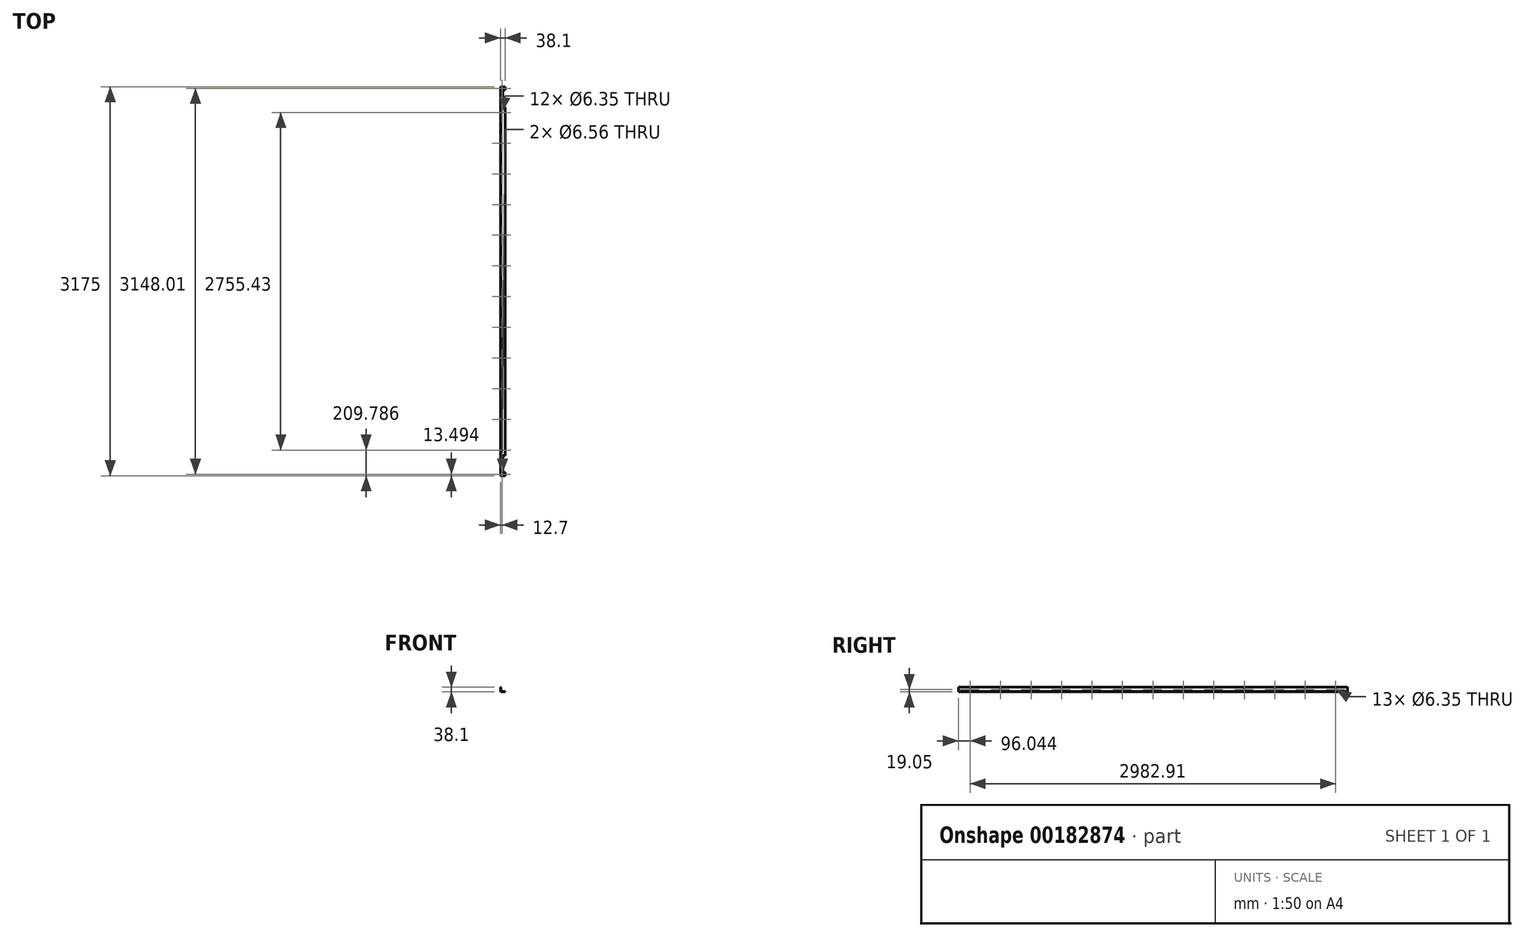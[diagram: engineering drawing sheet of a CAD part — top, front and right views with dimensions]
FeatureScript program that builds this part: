
annotation { "Feature Type Name" : "Feature", "Feature Type Description" : "" }
export const myFeature = defineFeature(function(context is Context, id is Id, definition is map)
    precondition{}
    {
        {
            var Q0;
            Q0=qCreatedBy(makeId("Front.planeOp"),FACE);
            var sketch = newSketch(context, id + "F0", { "sketchPlane" : qUnion([Q0])});
            skLineSegment(sketch, "E0.bottom", {"start": v(0, 0) * mm, "end": v(38.1, 0) * mm});
            skLineSegment(sketch, "E0.top", {"start": v(3.18, 3.17) * mm, "end": v(38.1, 3.17) * mm});
            skLineSegment(sketch, "E0.right", {"start": v(38.1, 0) * mm, "end": v(38.1, 3.17) * mm});
            skLineSegment(sketch, "E1.top", {"start": v(0, 38.1) * mm, "end": v(3.17, 38.1) * mm});
            skLineSegment(sketch, "E1.left", {"start": v(0, 0) * mm, "end": v(0, 38.1) * mm});
            skLineSegment(sketch, "E1.right", {"start": v(3.18, 3.17) * mm, "end": v(3.17, 38.1) * mm});
            skSolve(sketch);
        }
        {
            var Q0;
            Q0=makeQuery(id+"F0.imprint","IMPRINT",FACE,{"disambiguationData":[TD([[makeQuery(id+"F0.imprint","IMPRINT",EDGE,{"derivedFrom":sQuery(id+"F0.wireOp",EDGE,"E0.bottom")}),1.0]])]});
            extrude(context, id + "F1", {"entities" : qUnion([Q0]), "oppositeDirection" : true, "depth" : 3175 * mm});
        }
        {
            var Q0;
            Q0=qCreatedBy(makeId("Top.planeOp"),FACE);
            var sketch = newSketch(context, id + "F2", { "sketchPlane" : qUnion([Q0])});
            skLineSegment(sketch, "E2.bottom", {"start": v(38.1, 26.99) * mm, "end": v(20.64, 26.99) * mm});
            skLineSegment(sketch, "E2.top", {"start": v(38.1, 165.1) * mm, "end": v(20.64, 165.1) * mm});
            skLineSegment(sketch, "E2.left", {"start": v(38.1, 26.99) * mm, "end": v(38.1, 165.1) * mm});
            skLineSegment(sketch, "E2.right", {"start": v(20.64, 26.99) * mm, "end": v(20.64, 165.1) * mm});
            skCircle(sketch, "E3", {"center": v(12.7, 13.5) * mm, "radius": 3.28 * mm});
            skLineSegment(sketch, "E4", {"start": v(38.1, 1587.5) * mm, "end": v(-39.32, 1587.5) * mm, "construction": true});
            skLineSegment(sketch, "E5", {"start": v(20.64, 26.99) * mm, "end": v(20.64, 0) * mm, "construction": true});
            skLineSegment(sketch, "E6", {"start": v(49.67, 13.5) * mm, "end": v(-10.61, 13.5) * mm, "construction": true});
            skPoint(sketch, "E6.startSnap0", {"position": v(20.64, 13.5) * mm});
            skCircle(sketch, "E7.0.1.0", {"center": v(12.7, 209.79) * mm, "radius": 3.28 * mm});
            skCircle(sketch, "E7.0.2.0", {"center": v(12.7, 554.21) * mm, "radius": 3.28 * mm});
            skCircle(sketch, "E7.0.3.0", {"center": v(12.7, 898.64) * mm, "radius": 3.28 * mm});
            skCircle(sketch, "E7.0.4.0", {"center": v(12.7, 1243.07) * mm, "radius": 3.28 * mm});
            skCircle(sketch, "E7.0.5.0", {"center": v(12.7, 1587.5) * mm, "radius": 3.28 * mm});
            skLineSegment(sketch, "E7.direction1", {"start": v(12.7, 13.5) * mm, "end": v(55.73, 13.5) * mm, "construction": true});
            skLineSegment(sketch, "E7.direction2", {"start": v(12.7, 13.5) * mm, "end": v(12.7, 209.79) * mm, "construction": true});
            skLineSegment(sketch, "E8", {"start": v(12.7, 1587.5) * mm, "end": v(12.7, 1243.07) * mm});
            skLineSegment(sketch, "E9", {"start": v(12.7, 898.64) * mm, "end": v(12.7, 554.21) * mm});
            skLineSegment(sketch, "E10", {"start": v(12.7, 209.79) * mm, "end": v(12.7, 554.21) * mm});
            skLineSegment(sketch, "E11", {"start": v(12.7, 898.64) * mm, "end": v(12.7, 1243.07) * mm});
            skCircle(sketch, "E12.MirrorC", {"center": v(12.7, 1931.93) * mm, "radius": 3.28 * mm});
            skCircle(sketch, "E13.MirrorC", {"center": v(12.7, 2276.36) * mm, "radius": 3.28 * mm});
            skCircle(sketch, "E14.MirrorC", {"center": v(12.7, 2620.79) * mm, "radius": 3.28 * mm});
            skCircle(sketch, "E15.MirrorC", {"center": v(12.7, 2965.21) * mm, "radius": 3.28 * mm});
            skCircle(sketch, "E16.MirrorC", {"center": v(12.7, 3161.5) * mm, "radius": 3.28 * mm});
            skLineSegment(sketch, "E17.MirrorCS", {"start": v(38.1, 3148.01) * mm, "end": v(20.64, 3148.01) * mm});
            skLineSegment(sketch, "E18.MirrorCS", {"start": v(20.64, 3148.01) * mm, "end": v(20.64, 3009.9) * mm});
            skLineSegment(sketch, "E19.MirrorCS", {"start": v(38.1, 3148.01) * mm, "end": v(38.1, 3009.9) * mm});
            skLineSegment(sketch, "E20.MirrorCS", {"start": v(38.1, 3009.9) * mm, "end": v(20.64, 3009.9) * mm});
            skSolve(sketch);
        }
        {
            var Q0;
            Q0=qCreatedBy(makeId("Right.planeOp"),FACE);
            var sketch = newSketch(context, id + "F3", { "sketchPlane" : qUnion([Q0])});
            skLineSegment(sketch, "E21", {"start": v(57.42, 79.6) * mm, "end": v(57.42, -13.2) * mm, "construction": true});
            skCircle(sketch, "E22", {"center": v(79.28, 20.64) * mm, "radius": 3.18 * mm});
            skCircle(sketch, "E23", {"center": v(463.9, 20.64) * mm, "radius": 3.18 * mm});
            skLineSegment(sketch, "E24", {"start": v(838.44, 20.64) * mm, "end": v(463.9, 20.64) * mm, "construction": true});
            skLineSegment(sketch, "E25", {"start": v(838.44, 20.64) * mm, "end": v(1212.97, 20.64) * mm, "construction": true});
            skLineSegment(sketch, "E26", {"start": v(1212.97, 20.64) * mm, "end": v(1587.5, 20.64) * mm, "construction": true});
            skLineSegment(sketch, "E27", {"start": v(1587.5, 20.64) * mm, "end": v(1962.03, 20.64) * mm, "construction": true});
            skCircle(sketch, "E28", {"center": v(838.44, 20.64) * mm, "radius": 3.18 * mm});
            skCircle(sketch, "E29", {"center": v(1212.97, 20.64) * mm, "radius": 3.18 * mm});
            skCircle(sketch, "E30", {"center": v(1587.5, 20.64) * mm, "radius": 3.18 * mm});
            skCircle(sketch, "E31", {"center": v(1962.03, 20.64) * mm, "radius": 3.18 * mm});
            skLineSegment(sketch, "E32", {"start": v(1962.03, 20.64) * mm, "end": v(2336.56, 20.64) * mm, "construction": true});
            skLineSegment(sketch, "E33", {"start": v(2336.56, 20.64) * mm, "end": v(2730.13, 20.64) * mm, "construction": true});
            skCircle(sketch, "E34", {"center": v(2336.56, 20.64) * mm, "radius": 3.17 * mm});
            skCircle(sketch, "E35", {"center": v(2730.13, 20.64) * mm, "radius": 3.17 * mm});
            skLineSegment(sketch, "E36", {"start": v(3047.86, 3.17) * mm, "end": v(3047.86, 38.1) * mm, "construction": true});
            skLineSegment(sketch, "E37", {"start": v(2730.13, 20.64) * mm, "end": v(2903.64, 21.22) * mm});
            skSolve(sketch);
        }
        {
            var Q0;
            Q0=qCreatedBy(makeId("Right.planeOp"),FACE);
            var sketch = newSketch(context, id + "F4", { "sketchPlane" : qUnion([Q0])});
            skLineSegment(sketch, "E38", {"start": v(427.48, 19.05) * mm, "end": v(758.91, 19.05) * mm, "construction": true});
            skLineSegment(sketch, "E39", {"start": v(96.04, 19.05) * mm, "end": v(427.48, 19.05) * mm, "construction": true});
            skLineSegment(sketch, "E40", {"start": v(758.91, 19.05) * mm, "end": v(1090.35, 19.05) * mm, "construction": true});
            skLineSegment(sketch, "E41", {"start": v(1090.35, 19.05) * mm, "end": v(1421.78, 19.05) * mm, "construction": true});
            skLineSegment(sketch, "E42", {"start": v(1421.78, 19.05) * mm, "end": v(1753.22, 19.05) * mm, "construction": true});
            skLineSegment(sketch, "E43", {"start": v(1753.22, 19.05) * mm, "end": v(2084.65, 19.05) * mm, "construction": true});
            skLineSegment(sketch, "E44", {"start": v(2084.65, 19.05) * mm, "end": v(2416.09, 19.05) * mm, "construction": true});
            skLineSegment(sketch, "E45", {"start": v(2416.09, 19.05) * mm, "end": v(2747.52, 19.05) * mm, "construction": true});
            skLineSegment(sketch, "E46", {"start": v(96.04, 87.6) * mm, "end": v(3078.96, 87.6) * mm, "construction": true});
            skLineSegment(sketch, "E47", {"start": v(3078.96, -671.36) * mm, "end": v(3078.96, 846.57) * mm, "construction": true});
            skCircle(sketch, "E48", {"center": v(758.91, 19.05) * mm, "radius": 3.18 * mm});
            skCircle(sketch, "E49", {"center": v(427.48, 19.05) * mm, "radius": 3.18 * mm});
            skCircle(sketch, "E50", {"center": v(96.04, 19.05) * mm, "radius": 3.18 * mm});
            skCircle(sketch, "E51", {"center": v(1090.35, 19.05) * mm, "radius": 3.18 * mm});
            skCircle(sketch, "E52", {"center": v(1421.78, 19.05) * mm, "radius": 3.18 * mm});
            skCircle(sketch, "E53", {"center": v(1753.22, 19.05) * mm, "radius": 3.18 * mm});
            skCircle(sketch, "E54", {"center": v(2084.65, 19.05) * mm, "radius": 3.18 * mm});
            skCircle(sketch, "E55", {"center": v(2416.09, 19.05) * mm, "radius": 3.18 * mm});
            skCircle(sketch, "E56", {"center": v(2747.52, 19.05) * mm, "radius": 3.18 * mm});
            skLineSegment(sketch, "E57", {"start": v(1587.5, 87.6) * mm, "end": v(1587.5, 145.59) * mm});
            skLineSegment(sketch, "E58", {"start": v(2747.52, 19.05) * mm, "end": v(3078.96, 19.05) * mm, "construction": true});
            skCircle(sketch, "E59", {"center": v(3078.96, 19.05) * mm, "radius": 3.18 * mm});
            skLineSegment(sketch, "E60", {"start": v(96.04, 725.14) * mm, "end": v(96.04, -549.94) * mm, "construction": true});
            skLineSegment(sketch, "E61", {"start": v(42.9, 19.05) * mm, "end": v(-42.9, 19.05) * mm, "construction": true});
            skSolve(sketch);
        }
        {
            var Q0;
            Q0=qCreatedBy(makeId("Front.planeOp"),FACE);
            var sketch = newSketch(context, id + "F5", { "sketchPlane" : qUnion([Q0])});
            skLineSegment(sketch, "E62.bottom", {"start": v(43.8, 0.8) * mm, "end": v(81.9, 0.8) * mm});
            skLineSegment(sketch, "E62.top", {"start": v(46.97, 3.97) * mm, "end": v(81.9, 3.97) * mm});
            skLineSegment(sketch, "E62.right", {"start": v(81.9, 0.8) * mm, "end": v(81.9, 3.97) * mm});
            skLineSegment(sketch, "E63.top", {"start": v(43.8, 38.9) * mm, "end": v(46.97, 38.9) * mm});
            skLineSegment(sketch, "E63.left", {"start": v(43.8, 0.8) * mm, "end": v(43.8, 38.9) * mm});
            skLineSegment(sketch, "E63.right", {"start": v(46.97, 3.97) * mm, "end": v(46.97, 38.9) * mm});
            skSolve(sketch);
        }
        {
            var Q0;
            Q0=qCreatedBy(makeId("Top.planeOp"),FACE);
            var sketch = newSketch(context, id + "F6", { "sketchPlane" : qUnion([Q0])});
            skCircle(sketch, "E64", {"center": v(12.7, 209.79) * mm, "radius": 3.18 * mm});
            skCircle(sketch, "E65.0.1.0", {"center": v(12.7, 460.28) * mm, "radius": 3.18 * mm});
            skCircle(sketch, "E65.0.2.0", {"center": v(12.7, 710.77) * mm, "radius": 3.18 * mm});
            skCircle(sketch, "E65.0.3.0", {"center": v(12.7, 961.27) * mm, "radius": 3.18 * mm});
            skCircle(sketch, "E65.0.4.0", {"center": v(12.7, 1211.76) * mm, "radius": 3.18 * mm});
            skCircle(sketch, "E65.0.5.0", {"center": v(12.7, 1462.25) * mm, "radius": 3.18 * mm});
            skCircle(sketch, "E65.0.6.0", {"center": v(12.7, 1712.75) * mm, "radius": 3.18 * mm});
            skCircle(sketch, "E65.0.7.0", {"center": v(12.7, 1963.24) * mm, "radius": 3.18 * mm});
            skLineSegment(sketch, "E65.direction1", {"start": v(-272.76, 209.79) * mm, "end": v(12.7, 209.79) * mm, "construction": true});
            skLineSegment(sketch, "E65.direction2", {"start": v(12.7, 209.79) * mm, "end": v(12.7, 460.28) * mm, "construction": true});
            skCircle(sketch, "E66.0.0.8", {"center": v(12.7, 2213.73) * mm, "radius": 3.18 * mm});
            skCircle(sketch, "E66.0.0.9", {"center": v(12.7, 2464.23) * mm, "radius": 3.18 * mm});
            skCircle(sketch, "E66.0.0.10", {"center": v(12.7, 2714.72) * mm, "radius": 3.18 * mm});
            skCircle(sketch, "E66.0.0.11", {"center": v(12.7, 2965.21) * mm, "radius": 3.18 * mm});
            skSolve(sketch);
        }
        {
            var Q0;
            Q0=qCreatedBy(makeId("Right.planeOp"),FACE);
            var sketch = newSketch(context, id + "F7", { "sketchPlane" : qUnion([Q0])});
            skCircle(sketch, "E67", {"center": v(96.04, 19.05) * mm, "radius": 3.18 * mm});
            skLineSegment(sketch, "E68", {"start": v(96.04, -23.41) * mm, "end": v(96.04, 23.71) * mm, "construction": true});
            skLineSegment(sketch, "E69", {"start": v(26.2, 19.05) * mm, "end": v(-12.06, 19.05) * mm, "construction": true});
            skCircle(sketch, "E70.1.0.0", {"center": v(344.62, 19.05) * mm, "radius": 3.18 * mm});
            skCircle(sketch, "E70.2.0.0", {"center": v(593.2, 19.05) * mm, "radius": 3.18 * mm});
            skCircle(sketch, "E70.3.0.0", {"center": v(841.77, 19.05) * mm, "radius": 3.18 * mm});
            skCircle(sketch, "E70.4.0.0", {"center": v(1090.35, 19.05) * mm, "radius": 3.18 * mm});
            skCircle(sketch, "E70.5.0.0", {"center": v(1338.92, 19.05) * mm, "radius": 3.18 * mm});
            skCircle(sketch, "E70.6.0.0", {"center": v(1587.5, 19.05) * mm, "radius": 3.18 * mm});
            skCircle(sketch, "E70.7.0.0", {"center": v(1836.08, 19.05) * mm, "radius": 3.18 * mm});
            skLineSegment(sketch, "E70.direction1", {"start": v(96.04, 19.05) * mm, "end": v(344.62, 19.05) * mm, "construction": true});
            skLineSegment(sketch, "E71", {"start": v(3078.96, -4.4) * mm, "end": v(3078.96, 63.23) * mm, "construction": true});
            skCircle(sketch, "E72.0.8.0", {"center": v(2084.65, 19.05) * mm, "radius": 3.18 * mm});
            skCircle(sketch, "E72.0.9.0", {"center": v(2333.23, 19.05) * mm, "radius": 3.18 * mm});
            skCircle(sketch, "E72.0.10.0", {"center": v(2581.8, 19.05) * mm, "radius": 3.18 * mm});
            skCircle(sketch, "E73.0.11.0", {"center": v(2830.38, 19.05) * mm, "radius": 3.18 * mm});
            skCircle(sketch, "E74.0.12.0", {"center": v(3078.96, 19.05) * mm, "radius": 3.18 * mm});
            skSolve(sketch);
        }
        {
            var Q0;
            Q0=qCreatedBy(makeId("Top.planeOp"),FACE);
            var sketch = newSketch(context, id + "F8", { "sketchPlane" : qUnion([Q0])});
            skLineSegment(sketch, "E75.bottom", {"start": v(38.1, 26.99) * mm, "end": v(20.64, 26.99) * mm});
            skLineSegment(sketch, "E75.top", {"start": v(38.1, 165.1) * mm, "end": v(20.64, 165.1) * mm});
            skLineSegment(sketch, "E75.left", {"start": v(38.1, 26.99) * mm, "end": v(38.1, 165.1) * mm});
            skLineSegment(sketch, "E75.right", {"start": v(20.64, 26.99) * mm, "end": v(20.64, 165.1) * mm});
            skCircle(sketch, "E76", {"center": v(12.7, 13.5) * mm, "radius": 3.28 * mm});
            skLineSegment(sketch, "E77", {"start": v(20.64, 26.99) * mm, "end": v(20.64, 0) * mm, "construction": true});
            skPoint(sketch, "E78.startSnap0", {"position": v(20.64, 13.5) * mm});
            skLineSegment(sketch, "E79.direction1", {"start": v(12.7, 13.5) * mm, "end": v(51.26, 13.5) * mm, "construction": true});
            skLineSegment(sketch, "E80.MirrorCS", {"start": v(38.1, 3009.9) * mm, "end": v(20.64, 3009.9) * mm});
            skLineSegment(sketch, "E81.MirrorCS", {"start": v(20.64, 3148.01) * mm, "end": v(20.64, 3009.9) * mm});
            skLineSegment(sketch, "E82.MirrorCS", {"start": v(38.1, 3148.01) * mm, "end": v(20.64, 3148.01) * mm});
            skLineSegment(sketch, "E83.MirrorCS", {"start": v(38.1, 3148.01) * mm, "end": v(38.1, 3009.9) * mm});
            skCircle(sketch, "E84.MirrorC", {"center": v(12.7, 3161.5) * mm, "radius": 3.28 * mm});
            skSolve(sketch);
        }
        {
            var Q0;
            Q0 = qSketchRegion(id + "F6", true);
            var Q1;
            Q1 = qSketchRegion(id + "F8", true);
            extrude(context, id + "F9", {"entities" : qUnion([Q0, Q1]), "operationType" : NewBodyOperationType.REMOVE, "depth" : 25.4 * mm});
        }
        {
            var Q0;
            Q0 = qSketchRegion(id + "F7", true);
            extrude(context, id + "F10", {"entities" : qUnion([Q0]), "operationType" : NewBodyOperationType.REMOVE, "depth" : 25.4 * mm});
        }
    });
